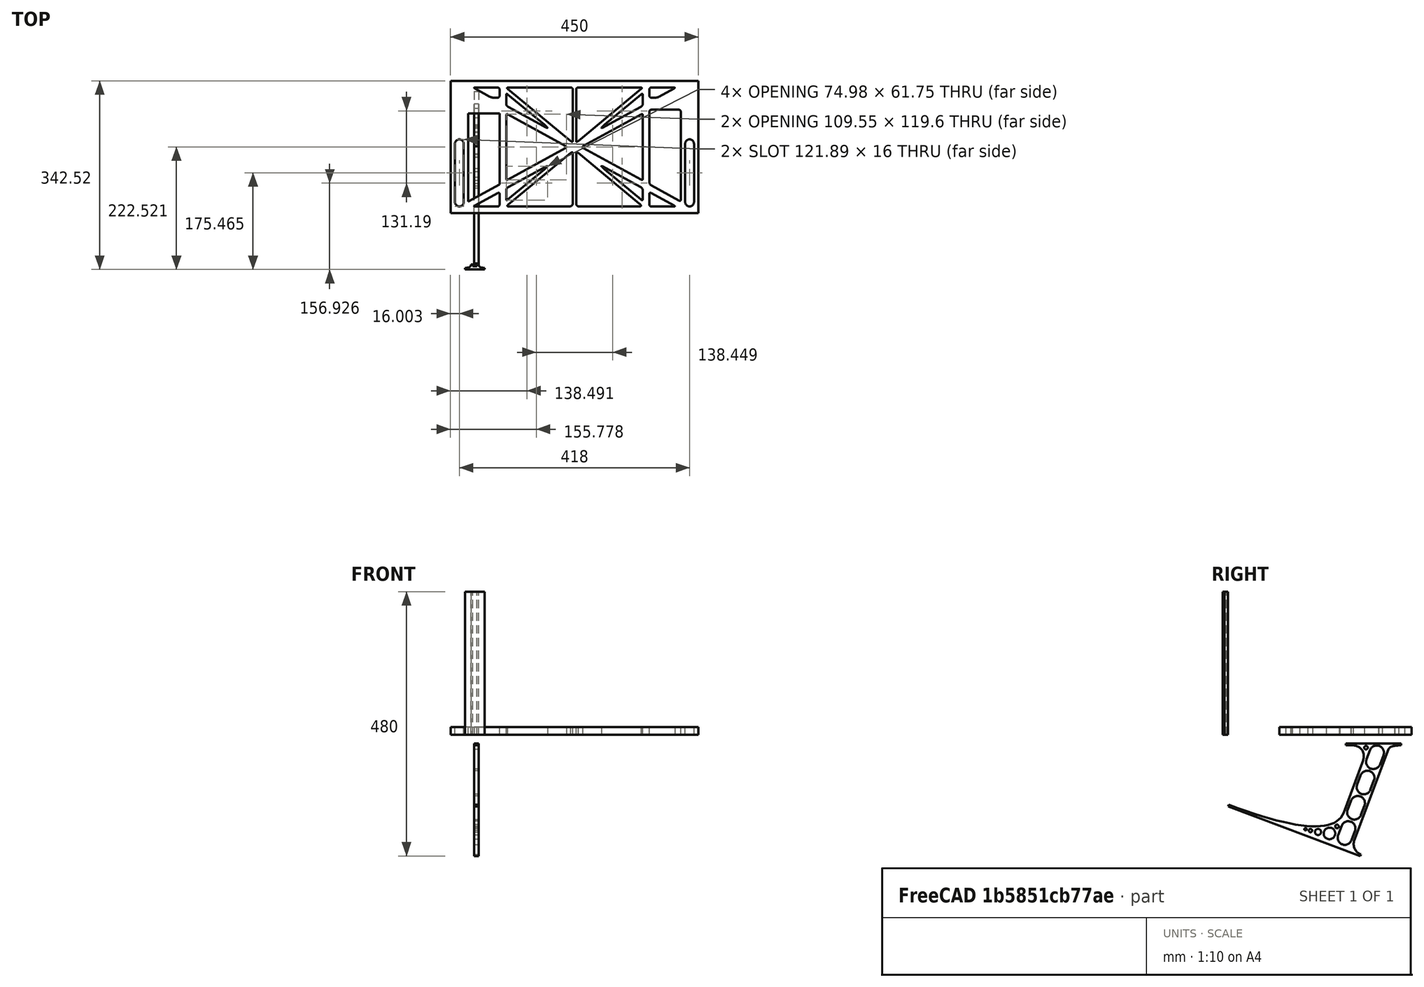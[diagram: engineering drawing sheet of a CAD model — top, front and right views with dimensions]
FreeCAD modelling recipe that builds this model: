
FCSTD DOCUMENT  (FreeCAD 0.19R0.19.2)
Label: laptopStand133FCStd
License: All rights reserved
LicenseURL: http://en.wikipedia.org/wiki/All_rights_reserved
objects: Sketcher::SketchObject×3, Part::Extrusion×3
note: 6 computed .brp shape members not serialized (recipe doc carries the construction recipe); baked Part::Feature solids carry a one-line shape summary decoded from their .brp

FEATURE [Sketcher::SketchObject] Sketch
  FullyConstrained = false
  sketch-geometry (349):
    g0: LineSegment StartX=-10.9272 StartY=-82.7794 StartZ=0 EndX=46.0728 EndY=-51.4823 EndZ=0
    g1: LineSegment StartX=-10.9272 StartY=76.4095 StartZ=0 EndX=-10.9272 EndY=-82.7794 EndZ=0
    g2: LineSegment StartX=46.0728 StartY=76.4095 StartZ=0 EndX=46.0728 EndY=-51.4823 EndZ=0
    g3: LineSegment StartX=-42.9272 StartY=136.221 StartZ=0 EndX=-42.9272 EndY=-103.779 EndZ=0
    g4: LineSegment StartX=407.073 StartY=136.221 StartZ=0 EndX=407.073 EndY=-103.779 EndZ=0
    g5: ArcOfCircle CenterX=-26.9272 CenterY=22.1087 CenterZ=0 NormalX=0 NormalY=0 NormalZ=1 AngleXU=0 Radius=8 StartAngle=1e-16 EndAngle=3.14159
    g6: ArcOfCircle CenterX=-26.9272 CenterY=-83.7794 CenterZ=0 NormalX=0 NormalY=0 NormalZ=1 AngleXU=0 Radius=8 StartAngle=3.14159 EndAngle=6.28319
    g7: LineSegment StartX=-34.9272 StartY=22.1087 StartZ=0 EndX=-34.9272 EndY=-83.7794 EndZ=0
    g8: LineSegment StartX=-18.9272 StartY=22.1087 StartZ=0 EndX=-18.9272 EndY=-83.7794 EndZ=0
    g9: ArcOfCircle CenterX=391.073 CenterY=22.1087 CenterZ=0 NormalX=0 NormalY=0 NormalZ=1 AngleXU=0 Radius=8 StartAngle=-4.4e-15 EndAngle=3.14159
    g10: LineSegment StartX=399.073 StartY=22.1087 StartZ=0 EndX=399.073 EndY=-83.7794 EndZ=0
    g11: LineSegment StartX=383.073 StartY=22.1087 StartZ=0 EndX=383.073 EndY=-83.7794 EndZ=0
    g12: ArcOfCircle CenterX=391.073 CenterY=-83.7794 CenterZ=0 NormalX=0 NormalY=0 NormalZ=1 AngleXU=0 Radius=8 StartAngle=3.14159 EndAngle=6.28319
    g13: Circle CenterX=175.022 CenterY=27.0628 CenterZ=0 NormalX=0 NormalY=0 NormalZ=1 AngleXU=0 Radius=1
    g14: Circle CenterX=179.022 CenterY=24.8665 CenterZ=0 NormalX=0 NormalY=0 NormalZ=1 AngleXU=0 Radius=1
    g15: Circle CenterX=179.022 CenterY=27.0628 CenterZ=0 NormalX=0 NormalY=0 NormalZ=1 AngleXU=0 Radius=1
    g16: BSplineCurve PolesCount=3 KnotsCount=2 Degree=2 IsPeriodic=0
    g17: GeomPoint X=175.022 Y=27.0628 Z=0
    g18: GeomPoint X=179.022 Y=27.0628 Z=0
    g19: Circle CenterX=189.124 CenterY=27.0628 CenterZ=0 NormalX=0 NormalY=0 NormalZ=1 AngleXU=0 Radius=1
    g20: Circle CenterX=185.124 CenterY=24.8665 CenterZ=0 NormalX=0 NormalY=0 NormalZ=1 AngleXU=0 Radius=1
    g21: Circle CenterX=185.124 CenterY=27.0628 CenterZ=0 NormalX=0 NormalY=0 NormalZ=1 AngleXU=0 Radius=1
    g22: BSplineCurve PolesCount=3 KnotsCount=2 Degree=2 IsPeriodic=0
    g23: GeomPoint X=189.124 Y=27.0628 Z=0
    g24: GeomPoint X=185.124 Y=27.0628 Z=0
    g25: Circle CenterX=175.022 CenterY=5.37834 CenterZ=0 NormalX=0 NormalY=0 NormalZ=1 AngleXU=0 Radius=1
    g26: Circle CenterX=179.022 CenterY=7.57463 CenterZ=0 NormalX=0 NormalY=0 NormalZ=1 AngleXU=0 Radius=1
    g27: Circle CenterX=179.022 CenterY=5.34704 CenterZ=0 NormalX=0 NormalY=0 NormalZ=1 AngleXU=0 Radius=1
    g28: BSplineCurve PolesCount=3 KnotsCount=2 Degree=2 IsPeriodic=0
    g29: GeomPoint X=175.022 Y=5.37834 Z=0
    g30: GeomPoint X=179.022 Y=5.34704 Z=0
    g31: Circle CenterX=189.124 CenterY=5.37834 CenterZ=0 NormalX=0 NormalY=0 NormalZ=1 AngleXU=0 Radius=1
    g32: Circle CenterX=185.124 CenterY=7.57463 CenterZ=0 NormalX=0 NormalY=0 NormalZ=1 AngleXU=0 Radius=1
    g33: Circle CenterX=185.124 CenterY=5.34704 CenterZ=0 NormalX=0 NormalY=0 NormalZ=1 AngleXU=0 Radius=1
    g34: BSplineCurve PolesCount=3 KnotsCount=2 Degree=2 IsPeriodic=0
    g35: GeomPoint X=189.124 Y=5.37834 Z=0
    g36: GeomPoint X=185.124 Y=5.34704 Z=0
    g37: Circle CenterX=165.871 CenterY=18.1458 CenterZ=0 NormalX=0 NormalY=0 NormalZ=1 AngleXU=0 Radius=1
    g38: Circle CenterX=169.377 CenterY=16.2206 CenterZ=0 NormalX=0 NormalY=0 NormalZ=1 AngleXU=0 Radius=1
    g39: Circle CenterX=165.871 CenterY=14.2954 CenterZ=0 NormalX=0 NormalY=0 NormalZ=1 AngleXU=0 Radius=1
    g40: BSplineCurve PolesCount=3 KnotsCount=2 Degree=2 IsPeriodic=0
    g41: GeomPoint X=165.871 Y=18.1458 Z=0
    g42: GeomPoint X=165.871 Y=14.2954 Z=0
    g43: Circle CenterX=198.275 CenterY=18.1458 CenterZ=0 NormalX=0 NormalY=0 NormalZ=1 AngleXU=0 Radius=1
    g44: Circle CenterX=194.768 CenterY=16.2206 CenterZ=0 NormalX=0 NormalY=0 NormalZ=1 AngleXU=0 Radius=1
    g45: Circle CenterX=198.275 CenterY=14.2954 CenterZ=0 NormalX=0 NormalY=0 NormalZ=1 AngleXU=0 Radius=1
    g46: BSplineCurve PolesCount=3 KnotsCount=2 Degree=2 IsPeriodic=0
    g47: GeomPoint X=198.275 Y=18.1458 Z=0
    g48: GeomPoint X=198.275 Y=14.2954 Z=0
    g49: LineSegment StartX=407.073 StartY=-103.779 StartZ=0 EndX=-42.9272 EndY=-103.779 EndZ=0
    g50: LineSegment StartX=407.073 StartY=136.221 StartZ=0 EndX=-42.9272 EndY=136.221 EndZ=0
    g51: LineSegment StartX=46.0728 StartY=76.4095 StartZ=0 EndX=-10.9272 EndY=76.4095 EndZ=0
    g52: Circle CenterX=125.607 CenterY=54.1951 CenterZ=0 NormalX=0 NormalY=0 NormalZ=1 AngleXU=0 Radius=1
    g53: Circle CenterX=139.632 CenterY=46.4944 CenterZ=0 NormalX=0 NormalY=0 NormalZ=1 AngleXU=0 Radius=1
    g54: Circle CenterX=127.326 CenterY=56.7187 CenterZ=0 NormalX=0 NormalY=0 NormalZ=1 AngleXU=0 Radius=1
    g55: BSplineCurve PolesCount=3 KnotsCount=2 Degree=2 IsPeriodic=0
    g56: GeomPoint X=125.607 Y=54.1951 Z=0
    g57: GeomPoint X=127.326 Y=56.7187 Z=0
    g58: Circle CenterX=236.821 CenterY=56.7187 CenterZ=0 NormalX=0 NormalY=0 NormalZ=1 AngleXU=0 Radius=1
    g59: Circle CenterX=224.513 CenterY=46.4944 CenterZ=0 NormalX=0 NormalY=0 NormalZ=1 AngleXU=0 Radius=1
    g60: Circle CenterX=238.538 CenterY=54.1951 CenterZ=0 NormalX=0 NormalY=0 NormalZ=1 AngleXU=0 Radius=1
    g61: BSplineCurve PolesCount=3 KnotsCount=2 Degree=2 IsPeriodic=0
    g62: GeomPoint X=236.821 Y=56.7187 Z=0
    g63: GeomPoint X=238.538 Y=54.1951 Z=0
    g64: Circle CenterX=238.538 CenterY=-21.7539 CenterZ=0 NormalX=0 NormalY=0 NormalZ=1 AngleXU=0 Radius=1
    g65: Circle CenterX=224.513 CenterY=-14.0532 CenterZ=0 NormalX=0 NormalY=0 NormalZ=1 AngleXU=0 Radius=1
    g66: Circle CenterX=236.821 CenterY=-24.2775 CenterZ=0 NormalX=0 NormalY=0 NormalZ=1 AngleXU=0 Radius=1
    g67: BSplineCurve PolesCount=3 KnotsCount=2 Degree=2 IsPeriodic=0
    g68: GeomPoint X=238.538 Y=-21.7539 Z=0
    g69: GeomPoint X=236.821 Y=-24.2775 Z=0
    g70: Circle CenterX=125.607 CenterY=-21.7539 CenterZ=0 NormalX=0 NormalY=0 NormalZ=1 AngleXU=0 Radius=1
    g71: Circle CenterX=139.632 CenterY=-14.0532 CenterZ=0 NormalX=0 NormalY=0 NormalZ=1 AngleXU=0 Radius=1
    g72: Circle CenterX=127.325 CenterY=-24.2775 CenterZ=0 NormalX=0 NormalY=0 NormalZ=1 AngleXU=0 Radius=1
    g73: BSplineCurve PolesCount=3 KnotsCount=2 Degree=2 IsPeriodic=0
    g74: GeomPoint X=125.607 Y=-21.7539 Z=0
    g75: GeomPoint X=127.325 Y=-24.2775 Z=0
    g76: Circle CenterX=302.996 CenterY=111.695 CenterZ=0 NormalX=0 NormalY=0 NormalZ=1 AngleXU=0 Radius=1
    g77: Circle CenterX=306.073 CenterY=114.251 CenterZ=0 NormalX=0 NormalY=0 NormalZ=1 AngleXU=0 Radius=1
    g78: Circle CenterX=306.073 CenterY=110.251 CenterZ=0 NormalX=0 NormalY=0 NormalZ=1 AngleXU=0 Radius=1
    g79: BSplineCurve PolesCount=3 KnotsCount=2 Degree=2 IsPeriodic=0
    g80: GeomPoint X=302.996 Y=111.695 Z=0
    g81: GeomPoint X=306.073 Y=110.251 Z=0
    g82: Circle CenterX=306.073 CenterY=95.2763 CenterZ=0 NormalX=0 NormalY=0 NormalZ=1 AngleXU=0 Radius=1
    g83: Circle CenterX=306.073 CenterY=91.2763 CenterZ=0 NormalX=0 NormalY=0 NormalZ=1 AngleXU=0 Radius=1
    g84: Circle CenterX=302.567 CenterY=89.3511 CenterZ=0 NormalX=0 NormalY=0 NormalZ=1 AngleXU=0 Radius=1
    g85: BSplineCurve PolesCount=3 KnotsCount=2 Degree=2 IsPeriodic=0
    g86: GeomPoint X=306.073 Y=95.2763 Z=0
    g87: GeomPoint X=302.567 Y=89.3511 Z=0
    g88: LineSegment StartX=306.073 StartY=110.251 StartZ=0 EndX=306.073 EndY=95.2763 EndZ=0
    g89: LineSegment StartX=302.996 StartY=111.695 StartZ=0 EndX=236.821 EndY=56.7187 EndZ=0
    g90: LineSegment StartX=238.538 StartY=54.1951 StartZ=0 EndX=302.567 EndY=89.3511 EndZ=0
    g91: Circle CenterX=61.1496 CenterY=111.695 CenterZ=0 NormalX=0 NormalY=0 NormalZ=1 AngleXU=0 Radius=1
    g92: Circle CenterX=58.0728 CenterY=114.251 CenterZ=0 NormalX=0 NormalY=0 NormalZ=1 AngleXU=0 Radius=1
    g93: Circle CenterX=58.0728 CenterY=110.251 CenterZ=0 NormalX=0 NormalY=0 NormalZ=1 AngleXU=0 Radius=1
    g94: BSplineCurve PolesCount=3 KnotsCount=2 Degree=2 IsPeriodic=0
    g95: GeomPoint X=61.1496 Y=111.695 Z=0
    g96: GeomPoint X=58.0728 Y=110.251 Z=0
    g97: Circle CenterX=61.5791 CenterY=89.3511 CenterZ=0 NormalX=0 NormalY=0 NormalZ=1 AngleXU=0 Radius=1
    g98: Circle CenterX=58.0728 CenterY=91.2763 CenterZ=0 NormalX=0 NormalY=0 NormalZ=1 AngleXU=0 Radius=1
    g99: Circle CenterX=58.0728 CenterY=95.2763 CenterZ=0 NormalX=0 NormalY=0 NormalZ=1 AngleXU=0 Radius=1
    g100: BSplineCurve PolesCount=3 KnotsCount=2 Degree=2 IsPeriodic=0
    g101: GeomPoint X=61.5791 Y=89.3511 Z=0
    g102: GeomPoint X=58.0728 Y=95.2763 Z=0
    g103: LineSegment StartX=58.0728 StartY=110.251 StartZ=0 EndX=58.0728 EndY=95.2763 EndZ=0
    g104: LineSegment StartX=61.1496 StartY=111.695 StartZ=0 EndX=127.326 EndY=56.7187 EndZ=0
    g105: LineSegment StartX=125.607 StartY=54.1951 StartZ=0 EndX=61.5791 EndY=89.3511 EndZ=0
    g106: Circle CenterX=61.5791 CenterY=-56.9099 CenterZ=0 NormalX=0 NormalY=0 NormalZ=1 AngleXU=0 Radius=1
    g107: Circle CenterX=58.0728 CenterY=-58.8351 CenterZ=0 NormalX=0 NormalY=0 NormalZ=1 AngleXU=0 Radius=1
    g108: Circle CenterX=58.0728 CenterY=-62.8351 CenterZ=0 NormalX=0 NormalY=0 NormalZ=1 AngleXU=0 Radius=1
    g109: BSplineCurve PolesCount=3 KnotsCount=2 Degree=2 IsPeriodic=0
    g110: GeomPoint X=61.5791 Y=-56.9099 Z=0
    g111: GeomPoint X=58.0728 Y=-62.8351 Z=0
    g112: Circle CenterX=58.0728 CenterY=-77.8102 CenterZ=0 NormalX=0 NormalY=0 NormalZ=1 AngleXU=0 Radius=1
    g113: Circle CenterX=58.0728 CenterY=-81.8102 CenterZ=0 NormalX=0 NormalY=0 NormalZ=1 AngleXU=0 Radius=1
    g114: Circle CenterX=61.1496 CenterY=-79.2541 CenterZ=0 NormalX=0 NormalY=0 NormalZ=1 AngleXU=0 Radius=1
    g115: BSplineCurve PolesCount=3 KnotsCount=2 Degree=2 IsPeriodic=0
    g116: GeomPoint X=58.0728 Y=-77.8102 Z=0
    g117: GeomPoint X=61.1496 Y=-79.2541 Z=0
    g118: LineSegment StartX=58.0728 StartY=-62.8351 StartZ=0 EndX=58.0728 EndY=-77.8102 EndZ=0
    g119: LineSegment StartX=61.1496 StartY=-79.2541 StartZ=0 EndX=127.325 EndY=-24.2775 EndZ=0
    g120: LineSegment StartX=125.607 StartY=-21.7539 StartZ=0 EndX=61.5791 EndY=-56.9099 EndZ=0
    g121: Circle CenterX=302.567 CenterY=-56.9099 CenterZ=0 NormalX=0 NormalY=0 NormalZ=1 AngleXU=0 Radius=1
    g122: Circle CenterX=306.073 CenterY=-58.8351 CenterZ=0 NormalX=0 NormalY=0 NormalZ=1 AngleXU=0 Radius=1
    g123: Circle CenterX=306.073 CenterY=-62.8351 CenterZ=0 NormalX=0 NormalY=0 NormalZ=1 AngleXU=0 Radius=1
    g124: BSplineCurve PolesCount=3 KnotsCount=2 Degree=2 IsPeriodic=0
    g125: GeomPoint X=302.567 Y=-56.9099 Z=0
    g126: GeomPoint X=306.073 Y=-62.8351 Z=0
    g127: Circle CenterX=302.996 CenterY=-79.2541 CenterZ=0 NormalX=0 NormalY=0 NormalZ=1 AngleXU=0 Radius=1
    g128: Circle CenterX=306.073 CenterY=-81.8102 CenterZ=0 NormalX=0 NormalY=0 NormalZ=1 AngleXU=0 Radius=1
    g129: Circle CenterX=306.073 CenterY=-77.8102 CenterZ=0 NormalX=0 NormalY=0 NormalZ=1 AngleXU=0 Radius=1
    g130: BSplineCurve PolesCount=3 KnotsCount=2 Degree=2 IsPeriodic=0
    g131: GeomPoint X=302.996 Y=-79.2541 Z=0
    g132: GeomPoint X=306.073 Y=-77.8102 Z=0
    g133: LineSegment StartX=306.073 StartY=-62.8351 StartZ=0 EndX=306.073 EndY=-77.8102 EndZ=0
    g134: LineSegment StartX=302.996 StartY=-79.2541 StartZ=0 EndX=236.821 EndY=-24.2775 EndZ=0
    g135: LineSegment StartX=238.538 StartY=-21.7539 StartZ=0 EndX=302.567 EndY=-56.9099 EndZ=0
    g136: Circle CenterX=61.6457 CenterY=-88.8112 CenterZ=0 NormalX=0 NormalY=0 NormalZ=1 AngleXU=0 Radius=1
    g137: Circle CenterX=58.0728 CenterY=-91.7794 CenterZ=0 NormalX=0 NormalY=0 NormalZ=1 AngleXU=0 Radius=1
    g138: Circle CenterX=63.9135 CenterY=-91.7794 CenterZ=0 NormalX=0 NormalY=0 NormalZ=1 AngleXU=0 Radius=1
    g139: BSplineCurve PolesCount=3 KnotsCount=2 Degree=2 IsPeriodic=0
    g140: GeomPoint X=61.6457 Y=-88.8112 Z=0
    g141: GeomPoint X=63.9135 Y=-91.7794 Z=0
    g142: Circle CenterX=179.022 CenterY=-85.8163 CenterZ=0 NormalX=0 NormalY=0 NormalZ=1 AngleXU=0 Radius=1
    g143: Circle CenterX=179.022 CenterY=-91.7794 CenterZ=0 NormalX=0 NormalY=0 NormalZ=1 AngleXU=0 Radius=1
    g144: Circle CenterX=171.895 CenterY=-91.7794 CenterZ=0 NormalX=0 NormalY=0 NormalZ=1 AngleXU=0 Radius=1
    g145: BSplineCurve PolesCount=3 KnotsCount=2 Degree=2 IsPeriodic=0
    g146: GeomPoint X=179.022 Y=-85.8163 Z=0
    g147: GeomPoint X=171.895 Y=-91.7794 Z=0
    g148: Circle CenterX=185.124 CenterY=-86.2028 CenterZ=0 NormalX=0 NormalY=0 NormalZ=1 AngleXU=0 Radius=1
    g149: Circle CenterX=185.124 CenterY=-91.7794 CenterZ=0 NormalX=0 NormalY=0 NormalZ=1 AngleXU=0 Radius=1
    g150: Circle CenterX=191.747 CenterY=-91.7794 CenterZ=0 NormalX=0 NormalY=0 NormalZ=1 AngleXU=0 Radius=1
    g151: BSplineCurve PolesCount=3 KnotsCount=2 Degree=2 IsPeriodic=0
    g152: GeomPoint X=185.124 Y=-86.2028 Z=0
    g153: GeomPoint X=191.747 Y=-91.7794 Z=0
    g154: Circle CenterX=299.888 CenterY=-86.6413 CenterZ=0 NormalX=0 NormalY=0 NormalZ=1 AngleXU=0 Radius=1
    g155: Circle CenterX=306.073 CenterY=-91.7794 CenterZ=0 NormalX=0 NormalY=0 NormalZ=1 AngleXU=0 Radius=1
    g156: Circle CenterX=298.776 CenterY=-91.7794 CenterZ=0 NormalX=0 NormalY=0 NormalZ=1 AngleXU=0 Radius=1
    g157: BSplineCurve PolesCount=3 KnotsCount=2 Degree=2 IsPeriodic=0
    g158: GeomPoint X=299.888 Y=-86.6413 Z=0
    g159: GeomPoint X=298.776 Y=-91.7794 Z=0
    g160: LineSegment StartX=189.124 StartY=5.37834 StartZ=0 EndX=299.888 EndY=-86.6413 EndZ=0
    g161: LineSegment StartX=298.776 StartY=-91.7794 StartZ=0 EndX=191.747 EndY=-91.7794 EndZ=0
    g162: LineSegment StartX=185.124 StartY=-86.2028 StartZ=0 EndX=185.124 EndY=5.34704 EndZ=0
    g163: LineSegment StartX=179.022 StartY=5.34704 StartZ=0 EndX=179.022 EndY=-85.8163 EndZ=0
    g164: LineSegment StartX=171.895 StartY=-91.7794 StartZ=0 EndX=63.9135 EndY=-91.7794 EndZ=0
    g165: LineSegment StartX=61.6457 StartY=-88.8112 StartZ=0 EndX=175.022 EndY=5.37834 EndZ=0
    g166: Circle CenterX=302.073 CenterY=124.221 CenterZ=0 NormalX=0 NormalY=0 NormalZ=1 AngleXU=0 Radius=1
    g167: Circle CenterX=306.073 CenterY=124.221 CenterZ=0 NormalX=0 NormalY=0 NormalZ=1 AngleXU=0 Radius=1
    g168: Circle CenterX=302.996 CenterY=121.665 CenterZ=0 NormalX=0 NormalY=0 NormalZ=1 AngleXU=0 Radius=1
    g169: BSplineCurve PolesCount=3 KnotsCount=2 Degree=2 IsPeriodic=0
    g170: GeomPoint X=302.073 Y=124.221 Z=0
    g171: GeomPoint X=302.996 Y=121.665 Z=0
    g172: Circle CenterX=189.124 CenterY=124.221 CenterZ=0 NormalX=0 NormalY=0 NormalZ=1 AngleXU=0 Radius=1
    g173: Circle CenterX=185.124 CenterY=124.221 CenterZ=0 NormalX=0 NormalY=0 NormalZ=1 AngleXU=0 Radius=1
    g174: Circle CenterX=185.124 CenterY=120.221 CenterZ=0 NormalX=0 NormalY=0 NormalZ=1 AngleXU=0 Radius=1
    g175: BSplineCurve PolesCount=3 KnotsCount=2 Degree=2 IsPeriodic=0
    g176: GeomPoint X=189.124 Y=124.221 Z=0
    g177: GeomPoint X=185.124 Y=120.221 Z=0
    g178: Circle CenterX=175.022 CenterY=124.221 CenterZ=0 NormalX=0 NormalY=0 NormalZ=1 AngleXU=0 Radius=1
    g179: Circle CenterX=179.022 CenterY=124.221 CenterZ=0 NormalX=0 NormalY=0 NormalZ=1 AngleXU=0 Radius=1
    g180: Circle CenterX=179.022 CenterY=120.221 CenterZ=0 NormalX=0 NormalY=0 NormalZ=1 AngleXU=0 Radius=1
    g181: BSplineCurve PolesCount=3 KnotsCount=2 Degree=2 IsPeriodic=0
    g182: GeomPoint X=175.022 Y=124.221 Z=0
    g183: GeomPoint X=179.022 Y=120.221 Z=0
    g184: Circle CenterX=62.0728 CenterY=124.221 CenterZ=0 NormalX=0 NormalY=0 NormalZ=1 AngleXU=0 Radius=1
    g185: Circle CenterX=58.0728 CenterY=124.221 CenterZ=0 NormalX=0 NormalY=0 NormalZ=1 AngleXU=0 Radius=1
    g186: Circle CenterX=61.1496 CenterY=121.665 CenterZ=0 NormalX=0 NormalY=0 NormalZ=1 AngleXU=0 Radius=1
    g187: BSplineCurve PolesCount=3 KnotsCount=2 Degree=2 IsPeriodic=0
    g188: GeomPoint X=62.0728 Y=124.221 Z=0
    g189: GeomPoint X=61.1496 Y=121.665 Z=0
    g190: LineSegment StartX=62.0728 StartY=124.221 StartZ=0 EndX=175.022 EndY=124.221 EndZ=0
    g191: LineSegment StartX=179.022 StartY=120.221 StartZ=0 EndX=179.022 EndY=27.0628 EndZ=0
    g192: LineSegment StartX=185.124 StartY=27.0628 StartZ=0 EndX=185.124 EndY=120.221 EndZ=0
    g193: LineSegment StartX=189.124 StartY=124.221 StartZ=0 EndX=302.073 EndY=124.221 EndZ=0
    g194: LineSegment StartX=302.996 StartY=121.665 StartZ=0 EndX=189.124 EndY=27.0628 EndZ=0
    g195: LineSegment StartX=175.022 StartY=27.0628 StartZ=0 EndX=61.1496 EndY=121.665 EndZ=0
    g196: Circle CenterX=61.5791 CenterY=75.4095 CenterZ=0 NormalX=0 NormalY=0 NormalZ=1 AngleXU=0 Radius=1
    g197: Circle CenterX=58.0728 CenterY=77.3346 CenterZ=0 NormalX=0 NormalY=0 NormalZ=1 AngleXU=0 Radius=1
    g198: Circle CenterX=58.0728 CenterY=73.3346 CenterZ=0 NormalX=0 NormalY=0 NormalZ=1 AngleXU=0 Radius=1
    g199: BSplineCurve PolesCount=3 KnotsCount=2 Degree=2 IsPeriodic=0
    g200: GeomPoint X=61.5791 Y=75.4095 Z=0
    g201: GeomPoint X=58.0728 Y=73.3346 Z=0
    g202: Circle CenterX=58.0728 CenterY=-40.8935 CenterZ=0 NormalX=0 NormalY=0 NormalZ=1 AngleXU=0 Radius=1
    g203: Circle CenterX=58.0728 CenterY=-44.8935 CenterZ=0 NormalX=0 NormalY=0 NormalZ=1 AngleXU=0 Radius=1
    g204: Circle CenterX=61.5791 CenterY=-42.9683 CenterZ=0 NormalX=0 NormalY=0 NormalZ=1 AngleXU=0 Radius=1
    g205: BSplineCurve PolesCount=3 KnotsCount=2 Degree=2 IsPeriodic=0
    g206: GeomPoint X=58.0728 Y=-40.8935 Z=0
    g207: GeomPoint X=61.5791 Y=-42.9683 Z=0
    g208: LineSegment StartX=61.5791 StartY=-42.9683 StartZ=0 EndX=165.871 EndY=14.2954 EndZ=0
    g209: LineSegment StartX=165.871 StartY=18.1458 StartZ=0 EndX=61.5791 EndY=75.4095 EndZ=0
    g210: LineSegment StartX=58.0728 StartY=73.3346 StartZ=0 EndX=58.0728 EndY=-40.8935 EndZ=0
    g211: Circle CenterX=302.567 CenterY=-42.9683 CenterZ=0 NormalX=0 NormalY=0 NormalZ=1 AngleXU=0 Radius=1
    g212: Circle CenterX=306.073 CenterY=-44.8935 CenterZ=0 NormalX=0 NormalY=0 NormalZ=1 AngleXU=0 Radius=1
    g213: Circle CenterX=306.073 CenterY=-40.8935 CenterZ=0 NormalX=0 NormalY=0 NormalZ=1 AngleXU=0 Radius=1
    g214: BSplineCurve PolesCount=3 KnotsCount=2 Degree=2 IsPeriodic=0
    g215: GeomPoint X=302.567 Y=-42.9683 Z=0
    g216: GeomPoint X=306.073 Y=-40.8935 Z=0
    g217: Circle CenterX=306.073 CenterY=73.3346 CenterZ=0 NormalX=0 NormalY=0 NormalZ=1 AngleXU=0 Radius=1
    g218: Circle CenterX=306.073 CenterY=77.3346 CenterZ=0 NormalX=0 NormalY=0 NormalZ=1 AngleXU=0 Radius=1
    g219: Circle CenterX=302.567 CenterY=75.4095 CenterZ=0 NormalX=0 NormalY=0 NormalZ=1 AngleXU=0 Radius=1
    g220: BSplineCurve PolesCount=3 KnotsCount=2 Degree=2 IsPeriodic=0
    g221: GeomPoint X=306.073 Y=73.3346 Z=0
    g222: GeomPoint X=302.567 Y=75.4095 Z=0
    g223: LineSegment StartX=302.567 StartY=-42.9683 StartZ=0 EndX=198.275 EndY=14.2954 EndZ=0
    g224: LineSegment StartX=198.275 StartY=18.1458 StartZ=0 EndX=302.567 EndY=75.4095 EndZ=0
    g225: LineSegment StartX=306.073 StartY=73.3346 StartZ=0 EndX=306.073 EndY=-40.8935 EndZ=0
    g226: LineSegment StartX=322.073 StartY=105.865 StartZ=0 EndX=328.643 EndY=105.865 EndZ=0
    g227: LineSegment StartX=318.073 StartY=120.221 StartZ=0 EndX=318.073 EndY=109.865 EndZ=0
    g228: LineSegment StartX=336.157 StartY=107.779 StartZ=0 EndX=362.567 EndY=122.294 EndZ=0
    g229: Circle CenterX=362.073 CenterY=124.221 CenterZ=0 NormalX=0 NormalY=0 NormalZ=1 AngleXU=0 Radius=1
    g230: Circle CenterX=366.073 CenterY=124.221 CenterZ=0 NormalX=0 NormalY=0 NormalZ=1 AngleXU=0 Radius=1
    g231: Circle CenterX=362.567 CenterY=122.294 CenterZ=0 NormalX=0 NormalY=0 NormalZ=1 AngleXU=0 Radius=1
    g232: BSplineCurve PolesCount=3 KnotsCount=2 Degree=2 IsPeriodic=0
    g233: GeomPoint X=362.073 Y=124.221 Z=0
    g234: GeomPoint X=362.567 Y=122.294 Z=0
    g235: Circle CenterX=322.073 CenterY=124.221 CenterZ=0 NormalX=0 NormalY=0 NormalZ=1 AngleXU=0 Radius=1
    g236: Circle CenterX=318.073 CenterY=124.221 CenterZ=0 NormalX=0 NormalY=0 NormalZ=1 AngleXU=0 Radius=1
    g237: Circle CenterX=318.073 CenterY=120.221 CenterZ=0 NormalX=0 NormalY=0 NormalZ=1 AngleXU=0 Radius=1
    g238: BSplineCurve PolesCount=3 KnotsCount=2 Degree=2 IsPeriodic=0
    g239: GeomPoint X=322.073 Y=124.221 Z=0
    g240: GeomPoint X=318.073 Y=120.221 Z=0
    g241: Circle CenterX=322.073 CenterY=105.865 CenterZ=0 NormalX=0 NormalY=0 NormalZ=1 AngleXU=0 Radius=1
    g242: Circle CenterX=318.073 CenterY=105.865 CenterZ=0 NormalX=0 NormalY=0 NormalZ=1 AngleXU=0 Radius=1
    g243: Circle CenterX=318.073 CenterY=109.865 CenterZ=0 NormalX=0 NormalY=0 NormalZ=1 AngleXU=0 Radius=1
    g244: BSplineCurve PolesCount=3 KnotsCount=2 Degree=2 IsPeriodic=0
    g245: GeomPoint X=322.073 Y=105.865 Z=0
    g246: GeomPoint X=318.073 Y=109.865 Z=0
    g247: Circle CenterX=336.157 CenterY=107.779 CenterZ=0 NormalX=0 NormalY=0 NormalZ=1 AngleXU=0 Radius=1
    g248: Circle CenterX=332.651 CenterY=105.853 CenterZ=0 NormalX=0 NormalY=0 NormalZ=1 AngleXU=0 Radius=1
    g249: Circle CenterX=328.643 CenterY=105.865 CenterZ=0 NormalX=0 NormalY=0 NormalZ=1 AngleXU=0 Radius=1
    g250: BSplineCurve PolesCount=3 KnotsCount=2 Degree=2 IsPeriodic=0
    g251: GeomPoint X=336.157 Y=107.779 Z=0
    g252: GeomPoint X=328.643 Y=105.865 Z=0
    g253: LineSegment StartX=322.073 StartY=124.221 StartZ=0 EndX=362.073 EndY=124.221 EndZ=0
    g254: Circle CenterX=371.567 CenterY=-80.8644 CenterZ=0 NormalX=0 NormalY=0 NormalZ=1 AngleXU=0 Radius=1
    g255: Circle CenterX=375.073 CenterY=-82.7896 CenterZ=0 NormalX=0 NormalY=0 NormalZ=1 AngleXU=0 Radius=1
    g256: Circle CenterX=375.073 CenterY=-78.7896 CenterZ=0 NormalX=0 NormalY=0 NormalZ=1 AngleXU=0 Radius=1
    g257: BSplineCurve PolesCount=3 KnotsCount=2 Degree=2 IsPeriodic=0
    g258: GeomPoint X=371.567 Y=-80.8644 Z=0
    g259: GeomPoint X=375.073 Y=-78.7896 Z=0
    g260: Circle CenterX=321.579 CenterY=-53.4075 CenterZ=0 NormalX=0 NormalY=0 NormalZ=1 AngleXU=0 Radius=1
    g261: Circle CenterX=318.073 CenterY=-51.4823 CenterZ=0 NormalX=0 NormalY=0 NormalZ=1 AngleXU=0 Radius=1
    g262: Circle CenterX=318.073 CenterY=-47.4823 CenterZ=0 NormalX=0 NormalY=0 NormalZ=1 AngleXU=0 Radius=1
    g263: BSplineCurve PolesCount=3 KnotsCount=2 Degree=2 IsPeriodic=0
    g264: GeomPoint X=321.579 Y=-53.4075 Z=0
    g265: GeomPoint X=318.073 Y=-47.4823 Z=0
    g266: LineSegment StartX=371.567 StartY=-80.8644 StartZ=0 EndX=321.579 EndY=-53.4075 EndZ=0
    g267: Circle CenterX=321.579 CenterY=-67.3492 CenterZ=0 NormalX=0 NormalY=0 NormalZ=1 AngleXU=0 Radius=1
    g268: Circle CenterX=318.073 CenterY=-65.424 CenterZ=0 NormalX=0 NormalY=0 NormalZ=1 AngleXU=0 Radius=1
    g269: Circle CenterX=318.073 CenterY=-69.424 CenterZ=0 NormalX=0 NormalY=0 NormalZ=1 AngleXU=0 Radius=1
    g270: BSplineCurve PolesCount=3 KnotsCount=2 Degree=2 IsPeriodic=0
    g271: GeomPoint X=321.579 Y=-67.3492 Z=0
    g272: GeomPoint X=318.073 Y=-69.424 Z=0
    g273: Circle CenterX=362.567 CenterY=-89.8542 CenterZ=0 NormalX=0 NormalY=0 NormalZ=1 AngleXU=0 Radius=1
    g274: Circle CenterX=366.073 CenterY=-91.7794 CenterZ=0 NormalX=0 NormalY=0 NormalZ=1 AngleXU=0 Radius=1
    g275: Circle CenterX=362.073 CenterY=-91.7794 CenterZ=0 NormalX=0 NormalY=0 NormalZ=1 AngleXU=0 Radius=1
    g276: BSplineCurve PolesCount=3 KnotsCount=2 Degree=2 IsPeriodic=0
    g277: GeomPoint X=362.567 Y=-89.8542 Z=0
    g278: GeomPoint X=362.073 Y=-91.7794 Z=0
    g279: Circle CenterX=322.073 CenterY=-91.7794 CenterZ=0 NormalX=0 NormalY=0 NormalZ=1 AngleXU=0 Radius=1
    g280: Circle CenterX=318.073 CenterY=-91.7794 CenterZ=0 NormalX=0 NormalY=0 NormalZ=1 AngleXU=0 Radius=1
    g281: Circle CenterX=318.073 CenterY=-87.7794 CenterZ=0 NormalX=0 NormalY=0 NormalZ=1 AngleXU=0 Radius=1
    g282: BSplineCurve PolesCount=3 KnotsCount=2 Degree=2 IsPeriodic=0
    g283: GeomPoint X=322.073 Y=-91.7794 Z=0
    g284: GeomPoint X=318.073 Y=-87.7794 Z=0
    g285: LineSegment StartX=362.567 StartY=-89.8542 StartZ=0 EndX=321.579 EndY=-67.3492 EndZ=0
    g286: LineSegment StartX=318.073 StartY=-69.424 StartZ=0 EndX=318.073 EndY=-87.7794 EndZ=0
    g287: LineSegment StartX=322.073 StartY=-91.7794 StartZ=0 EndX=362.073 EndY=-91.7794 EndZ=0
    g288: Circle CenterX=2.07281 CenterY=124.221 CenterZ=0 NormalX=0 NormalY=0 NormalZ=1 AngleXU=0 Radius=1
    g289: Circle CenterX=1.57905 CenterY=122.295 CenterZ=0 NormalX=0 NormalY=0 NormalZ=1 AngleXU=0 Radius=1
    g290: BSplineCurve PolesCount=3 KnotsCount=2 Degree=2 IsPeriodic=0
    g291: GeomPoint X=2.07281 Y=124.221 Z=0
    g292: GeomPoint X=1.57905 Y=122.295 Z=0
    g293: Circle CenterX=42.0728 CenterY=124.221 CenterZ=0 NormalX=0 NormalY=0 NormalZ=1 AngleXU=0 Radius=1
    g294: Circle CenterX=46.0728 CenterY=124.221 CenterZ=0 NormalX=0 NormalY=0 NormalZ=1 AngleXU=0 Radius=1
    g295: Circle CenterX=46.0728 CenterY=120.221 CenterZ=0 NormalX=0 NormalY=0 NormalZ=1 AngleXU=0 Radius=1
    g296: BSplineCurve PolesCount=3 KnotsCount=2 Degree=2 IsPeriodic=0
    g297: GeomPoint X=42.0728 Y=124.221 Z=0
    g298: GeomPoint X=46.0728 Y=120.221 Z=0
    g299: Circle CenterX=46.0728 CenterY=109.865 CenterZ=0 NormalX=0 NormalY=0 NormalZ=1 AngleXU=0 Radius=1
    g300: Circle CenterX=46.0728 CenterY=105.865 CenterZ=0 NormalX=0 NormalY=0 NormalZ=1 AngleXU=0 Radius=1
    g301: Circle CenterX=42.0728 CenterY=105.865 CenterZ=0 NormalX=0 NormalY=0 NormalZ=1 AngleXU=0 Radius=1
    g302: BSplineCurve PolesCount=3 KnotsCount=2 Degree=2 IsPeriodic=0
    g303: GeomPoint X=46.0728 Y=109.865 Z=0
    g304: GeomPoint X=42.0728 Y=105.865 Z=0
    g305: Circle CenterX=35.5028 CenterY=105.865 CenterZ=0 NormalX=0 NormalY=0 NormalZ=1 AngleXU=0 Radius=1
    g306: Circle CenterX=31.5028 CenterY=105.865 CenterZ=0 NormalX=0 NormalY=0 NormalZ=1 AngleXU=0 Radius=1
    g307: Circle CenterX=27.9965 CenterY=107.79 CenterZ=0 NormalX=0 NormalY=0 NormalZ=1 AngleXU=0 Radius=1
    g308: BSplineCurve PolesCount=3 KnotsCount=2 Degree=2 IsPeriodic=0
    g309: GeomPoint X=35.5028 Y=105.865 Z=0
    g310: GeomPoint X=27.9965 Y=107.79 Z=0
    g311: LineSegment StartX=2.07281 StartY=124.221 StartZ=0 EndX=42.0728 EndY=124.221 EndZ=0
    g312: LineSegment StartX=46.0728 StartY=120.221 StartZ=0 EndX=46.0728 EndY=109.865 EndZ=0
    g313: LineSegment StartX=42.0728 StartY=105.865 StartZ=0 EndX=35.5028 EndY=105.865 EndZ=0
    g314: LineSegment StartX=27.9965 StartY=107.79 StartZ=0 EndX=1.57905 EndY=122.295 EndZ=0
    g315: Circle CenterX=42.5666 CenterY=-67.3492 CenterZ=0 NormalX=0 NormalY=0 NormalZ=1 AngleXU=0 Radius=1
    g316: Circle CenterX=46.0728 CenterY=-65.424 CenterZ=0 NormalX=0 NormalY=0 NormalZ=1 AngleXU=0 Radius=1
    g317: Circle CenterX=46.0728 CenterY=-69.424 CenterZ=0 NormalX=0 NormalY=0 NormalZ=1 AngleXU=0 Radius=1
    g318: BSplineCurve PolesCount=3 KnotsCount=2 Degree=2 IsPeriodic=0
    g319: GeomPoint X=42.5666 Y=-67.3492 Z=0
    g320: GeomPoint X=46.0728 Y=-69.424 Z=0
    g321: Circle CenterX=46.0728 CenterY=-87.7794 CenterZ=0 NormalX=0 NormalY=0 NormalZ=1 AngleXU=0 Radius=1
    g322: Circle CenterX=46.0728 CenterY=-91.7794 CenterZ=0 NormalX=0 NormalY=0 NormalZ=1 AngleXU=0 Radius=1
    g323: Circle CenterX=42.0728 CenterY=-91.7794 CenterZ=0 NormalX=0 NormalY=0 NormalZ=1 AngleXU=0 Radius=1
    g324: BSplineCurve PolesCount=3 KnotsCount=2 Degree=2 IsPeriodic=0
    g325: GeomPoint X=46.0728 Y=-87.7794 Z=0
    g326: GeomPoint X=42.0728 Y=-91.7794 Z=0
    g327: Circle CenterX=2.07281 CenterY=-91.7794 CenterZ=0 NormalX=0 NormalY=0 NormalZ=1 AngleXU=0 Radius=1
    g328: Circle CenterX=-1.92719 CenterY=-91.7794 CenterZ=0 NormalX=0 NormalY=0 NormalZ=1 AngleXU=0 Radius=1
    g329: Circle CenterX=1.57905 CenterY=-89.8542 CenterZ=0 NormalX=0 NormalY=0 NormalZ=1 AngleXU=0 Radius=1
    g330: BSplineCurve PolesCount=3 KnotsCount=2 Degree=2 IsPeriodic=0
    g331: GeomPoint X=2.07281 Y=-91.7794 Z=0
    g332: GeomPoint X=1.57905 Y=-89.8542 Z=0
    g333: LineSegment StartX=2.07281 StartY=-91.7794 StartZ=0 EndX=42.0728 EndY=-91.7794 EndZ=0
    g334: LineSegment StartX=46.0728 StartY=-87.7794 StartZ=0 EndX=46.0728 EndY=-69.424 EndZ=0
    g335: LineSegment StartX=42.5666 StartY=-67.3492 StartZ=0 EndX=1.57905 EndY=-89.8542 EndZ=0
    g336: LineSegment StartX=375.073 StartY=76.4095 StartZ=0 EndX=375.073 EndY=-78.7896 EndZ=0
    g337: Circle CenterX=322.073 CenterY=76.4095 CenterZ=0 NormalX=0 NormalY=0 NormalZ=1 AngleXU=0 Radius=4
    g338: BSplineCurve PolesCount=3 KnotsCount=2 Degree=2 IsPeriodic=0
    g339: GeomPoint X=318.073 Y=72.4095 Z=0
    g340: GeomPoint X=322.073 Y=76.4095 Z=0
    g341: LineSegment StartX=371.073 StartY=76.4095 StartZ=0 EndX=375.073 EndY=76.4095 EndZ=0
    g342: Circle CenterX=375.073 CenterY=72.4095 CenterZ=0 NormalX=0 NormalY=0 NormalZ=1 AngleXU=0 Radius=1
    g343: Circle CenterX=375.073 CenterY=76.4095 CenterZ=0 NormalX=0 NormalY=0 NormalZ=1 AngleXU=0 Radius=1
    g344: Circle CenterX=371.073 CenterY=76.4095 CenterZ=0 NormalX=0 NormalY=0 NormalZ=1 AngleXU=0 Radius=1
    g345: BSplineCurve PolesCount=3 KnotsCount=2 Degree=2 IsPeriodic=0
    g346: GeomPoint X=375.073 Y=72.4095 Z=0
    g347: GeomPoint X=371.073 Y=76.4095 Z=0
    g348: LineSegment StartX=322.073 StartY=76.4095 StartZ=0 EndX=371.073 EndY=76.4095 EndZ=0
  constraints (575):
    c: Coincident(g0,g2)
    c: Block(g0)
    c: Block(g1)
    c: Vertical(g3)
    c: Vertical(g4)
    c: Block(g4)
    c: Block(g3)
    c: Tangent(g5,g8) = 1.5708
    c: Tangent(g5,g7) = -1.5708
    c: Tangent(g7,g6) = -1.5708
    c: Tangent(g8,g6) = 1.5708
    c: Vertical(g7)
    c: Equal(g5,g6)
    c: Block(g8)
    c: Block(g7)
    c: Tangent(g9,g10) = 1.5708
    c: Tangent(g10,g12) = 1.5708
    c: Equal(g9,g12)
    c: Coincident(g11,g9)
    c: Coincident(g11,g12)
    c: Block(g10)
    c: Block(g11)
    c: Weight(g13) = 1
    c: Equal(g13,g14)
    c: Equal(g13,g15)
    c: InternalAlignment(g13,g16)
    c: InternalAlignment(g14,g16)
    c: InternalAlignment(g15,g16)
    c: InternalAlignment(g17,g16)
    c: InternalAlignment(g18,g16)
    c: Weight(g19) = 1
    c: Equal(g19,g20)
    c: Equal(g19,g21)
    c: InternalAlignment(g19,g22)
    c: InternalAlignment(g20,g22)
    c: InternalAlignment(g21,g22)
    c: InternalAlignment(g23,g22)
    c: InternalAlignment(g24,g22)
    c: Block(g22)
    c: Block(g16)
    c: Weight(g25) = 1
    c: Equal(g25,g26)
    c: Equal(g25,g27)
    c: InternalAlignment(g25,g28)
    c: InternalAlignment(g26,g28)
    c: InternalAlignment(g27,g28)
    c: InternalAlignment(g29,g28)
    c: InternalAlignment(g30,g28)
    c: Weight(g31) = 1
    c: Equal(g31,g32)
    c: Equal(g31,g33)
    c: InternalAlignment(g31,g34)
    c: InternalAlignment(g32,g34)
    c: InternalAlignment(g33,g34)
    c: InternalAlignment(g35,g34)
    c: InternalAlignment(g36,g34)
    c: Block(g34)
    c: Block(g28)
    c: Weight(g37) = 1
    c: Equal(g37,g38)
    c: Equal(g37,g39)
    c: InternalAlignment(g37,g40)
    c: InternalAlignment(g38,g40)
    c: InternalAlignment(g39,g40)
    c: InternalAlignment(g41,g40)
    c: InternalAlignment(g42,g40)
    c: Weight(g43) = 1
    c: Equal(g43,g44)
    c: Equal(g43,g45)
    c: InternalAlignment(g43,g46)
    c: InternalAlignment(g44,g46)
    c: InternalAlignment(g45,g46)
    c: InternalAlignment(g47,g46)
    c: InternalAlignment(g48,g46)
    c: Block(g40)
    c: Block(g46)
    c: Coincident(g49,g4)
    c: Coincident(g49,g3)
    c: Horizontal(g49)
    c: Distance(g49) = 450
    c: Coincident(g50,g4)
    c: Coincident(g50,g3)
    c: Horizontal(g50)
    c: Horizontal(g51)
    c: Coincident(g2,g51)
    c: Block(g51)
    c: Coincident(g1,g51)
    c: Weight(g52) = 1
    c: Equal(g52,g53)
    c: Equal(g52,g54)
    c: InternalAlignment(g52,g55)
    c: InternalAlignment(g53,g55)
    c: InternalAlignment(g54,g55)
    c: InternalAlignment(g56,g55)
    c: InternalAlignment(g57,g55)
    c: Block(g55)
    c: Weight(g58) = 1
    c: Equal(g58,g59)
    c: Equal(g58,g60)
    c: InternalAlignment(g58,g61)
    c: InternalAlignment(g59,g61)
    c: InternalAlignment(g60,g61)
    c: InternalAlignment(g62,g61)
    c: InternalAlignment(g63,g61)
    c: Block(g61)
    c: Weight(g64) = 1
    c: Equal(g64,g65)
    c: Equal(g64,g66)
    c: InternalAlignment(g64,g67)
    c: InternalAlignment(g65,g67)
    c: InternalAlignment(g66,g67)
    c: InternalAlignment(g68,g67)
    c: InternalAlignment(g69,g67)
    c: Block(g67)
    c: Weight(g70) = 1
    c: Equal(g70,g71)
    c: Equal(g70,g72)
    c: InternalAlignment(g70,g73)
    c: InternalAlignment(g71,g73)
    c: InternalAlignment(g72,g73)
    c: InternalAlignment(g74,g73)
    c: InternalAlignment(g75,g73)
    c: Block(g73)
    c: Weight(g76) = 1
    c: Equal(g76,g77)
    c: Equal(g76,g78)
    c: InternalAlignment(g76,g79)
    c: InternalAlignment(g77,g79)
    c: InternalAlignment(g78,g79)
    c: InternalAlignment(g80,g79)
    c: InternalAlignment(g81,g79)
    c: Weight(g82) = 1
    c: Equal(g82,g83)
    c: Equal(g82,g84)
    c: InternalAlignment(g82,g85)
    c: InternalAlignment(g83,g85)
    c: InternalAlignment(g84,g85)
    c: InternalAlignment(g86,g85)
    c: InternalAlignment(g87,g85)
    c: Block(g79)
    c: Block(g85)
    c: Coincident(g88,g79)
    c: Coincident(g88,g85)
    c: Vertical(g88)
    c: Coincident(g89,g79)
    c: Coincident(g89,g61)
    c: Coincident(g90,g61)
    c: Coincident(g90,g85)
    c: Weight(g91) = 1
    c: Equal(g91,g92)
    c: Equal(g91,g93)
    c: InternalAlignment(g91,g94)
    c: InternalAlignment(g92,g94)
    c: InternalAlignment(g93,g94)
    c: InternalAlignment(g95,g94)
    c: InternalAlignment(g96,g94)
    c: Weight(g97) = 1
    c: Equal(g97,g98)
    c: Equal(g97,g99)
    c: InternalAlignment(g97,g100)
    c: InternalAlignment(g98,g100)
    c: InternalAlignment(g99,g100)
    c: InternalAlignment(g101,g100)
    c: InternalAlignment(g102,g100)
    c: Block(g94)
    c: Block(g100)
    c: Coincident(g103,g94)
    c: Coincident(g103,g100)
    c: Vertical(g103)
    c: Coincident(g104,g94)
    c: Coincident(g104,g55)
    c: Coincident(g105,g55)
    c: Coincident(g105,g100)
    c: Weight(g106) = 1
    c: Equal(g106,g107)
    c: Equal(g106,g108)
    c: InternalAlignment(g106,g109)
    c: InternalAlignment(g107,g109)
    c: InternalAlignment(g108,g109)
    c: InternalAlignment(g110,g109)
    c: InternalAlignment(g111,g109)
    c: Weight(g112) = 1
    c: Equal(g112,g113)
    c: Equal(g112,g114)
    c: InternalAlignment(g112,g115)
    c: InternalAlignment(g113,g115)
    c: InternalAlignment(g114,g115)
    c: InternalAlignment(g116,g115)
    c: InternalAlignment(g117,g115)
    c: Block(g109)
    c: Block(g115)
    c: Coincident(g118,g109)
    c: Coincident(g118,g115)
    c: Vertical(g118)
    c: Coincident(g119,g115)
    c: Coincident(g119,g73)
    c: Coincident(g120,g73)
    c: Coincident(g120,g109)
    c: Weight(g121) = 1
    c: Equal(g121,g122)
    c: Equal(g121,g123)
    c: InternalAlignment(g121,g124)
    c: InternalAlignment(g122,g124)
    c: InternalAlignment(g123,g124)
    c: InternalAlignment(g125,g124)
    c: InternalAlignment(g126,g124)
    c: Weight(g127) = 1
    c: Equal(g127,g128)
    c: Equal(g127,g129)
    c: InternalAlignment(g127,g130)
    c: InternalAlignment(g128,g130)
    c: InternalAlignment(g129,g130)
    c: InternalAlignment(g131,g130)
    c: InternalAlignment(g132,g130)
    c: Block(g124)
    c: Block(g130)
    c: Coincident(g133,g124)
    c: Coincident(g133,g130)
    c: Vertical(g133)
    c: Coincident(g134,g130)
    c: Coincident(g134,g67)
    c: Coincident(g135,g67)
    c: Coincident(g135,g124)
    c: Weight(g136) = 1
    c: Equal(g136,g137)
    c: Equal(g136,g138)
    c: InternalAlignment(g136,g139)
    c: InternalAlignment(g137,g139)
    c: InternalAlignment(g138,g139)
    c: InternalAlignment(g140,g139)
    c: InternalAlignment(g141,g139)
    c: Weight(g142) = 1
    c: Equal(g142,g143)
    c: Equal(g142,g144)
    c: InternalAlignment(g142,g145)
    c: InternalAlignment(g143,g145)
    c: InternalAlignment(g144,g145)
    c: InternalAlignment(g146,g145)
    c: InternalAlignment(g147,g145)
    c: Weight(g148) = 1
    c: Equal(g148,g149)
    c: Equal(g148,g150)
    c: InternalAlignment(g148,g151)
    c: InternalAlignment(g149,g151)
    c: InternalAlignment(g150,g151)
    c: InternalAlignment(g152,g151)
    c: InternalAlignment(g153,g151)
    c: Weight(g154) = 1
    c: Equal(g154,g155)
    c: Equal(g154,g156)
    c: InternalAlignment(g154,g157)
    c: InternalAlignment(g155,g157)
    c: InternalAlignment(g156,g157)
    c: InternalAlignment(g158,g157)
    c: InternalAlignment(g159,g157)
    c: Block(g157)
    c: Block(g151)
    c: Block(g145)
    c: Block(g139)
    c: Coincident(g160,g34)
    c: Coincident(g160,g157)
    c: Coincident(g161,g157)
    c: Coincident(g161,g151)
    c: Horizontal(g161)
    c: Coincident(g162,g151)
    c: Coincident(g162,g34)
    c: Vertical(g162)
    c: Coincident(g163,g28)
    c: Coincident(g163,g145)
    c: Vertical(g163)
    c: Coincident(g164,g145)
    c: Coincident(g164,g139)
    c: Horizontal(g164)
    c: Coincident(g165,g139)
    c: Coincident(g165,g28)
    c: Weight(g166) = 1
    c: Equal(g166,g167)
    c: Equal(g166,g168)
    c: InternalAlignment(g166,g169)
    c: InternalAlignment(g167,g169)
    c: InternalAlignment(g168,g169)
    c: InternalAlignment(g170,g169)
    c: InternalAlignment(g171,g169)
    c: Weight(g172) = 1
    c: Equal(g172,g173)
    c: Equal(g172,g174)
    c: InternalAlignment(g172,g175)
    c: InternalAlignment(g173,g175)
    c: InternalAlignment(g174,g175)
    c: InternalAlignment(g176,g175)
    c: InternalAlignment(g177,g175)
    c: Weight(g178) = 1
    c: Equal(g178,g179)
    c: Equal(g178,g180)
    c: InternalAlignment(g178,g181)
    c: InternalAlignment(g179,g181)
    c: InternalAlignment(g180,g181)
    c: InternalAlignment(g182,g181)
    c: InternalAlignment(g183,g181)
    c: Weight(g184) = 1
    c: Equal(g184,g185)
    c: Equal(g184,g186)
    c: InternalAlignment(g184,g187)
    c: InternalAlignment(g185,g187)
    c: InternalAlignment(g186,g187)
    c: InternalAlignment(g188,g187)
    c: InternalAlignment(g189,g187)
    c: Block(g187)
    c: Block(g181)
    c: Block(g175)
    c: Block(g169)
    c: Coincident(g190,g187)
    c: Coincident(g190,g181)
    c: Horizontal(g190)
    c: Coincident(g191,g181)
    c: Coincident(g191,g16)
    c: Vertical(g191)
    c: Coincident(g192,g22)
    c: Coincident(g192,g175)
    c: Vertical(g192)
    c: Coincident(g193,g175)
    c: Coincident(g193,g169)
    c: Horizontal(g193)
    c: Coincident(g194,g169)
    c: Coincident(g194,g22)
    c: Coincident(g195,g16)
    c: Weight(g196) = 1
    c: Equal(g196,g197)
    c: Equal(g196,g198)
    c: InternalAlignment(g196,g199)
    c: InternalAlignment(g197,g199)
    c: InternalAlignment(g198,g199)
    c: InternalAlignment(g200,g199)
    c: InternalAlignment(g201,g199)
    c: Weight(g202) = 1
    c: Equal(g202,g203)
    c: Equal(g202,g204)
    c: InternalAlignment(g202,g205)
    c: InternalAlignment(g203,g205)
    c: InternalAlignment(g204,g205)
    c: InternalAlignment(g206,g205)
    c: InternalAlignment(g207,g205)
    c: Block(g205)
    c: Block(g199)
    c: Coincident(g208,g205)
    c: Coincident(g208,g40)
    c: Coincident(g209,g40)
    c: Coincident(g209,g199)
    c: Coincident(g210,g199)
    c: Coincident(g210,g205)
    c: Vertical(g210)
    c: Weight(g211) = 1
    c: Equal(g211,g212)
    c: Equal(g211,g213)
    c: InternalAlignment(g211,g214)
    c: InternalAlignment(g212,g214)
    c: InternalAlignment(g213,g214)
    c: InternalAlignment(g215,g214)
    c: InternalAlignment(g216,g214)
    c: Weight(g217) = 1
    c: Equal(g217,g218)
    c: Equal(g217,g219)
    c: InternalAlignment(g217,g220)
    c: InternalAlignment(g218,g220)
    c: InternalAlignment(g219,g220)
    c: InternalAlignment(g221,g220)
    c: InternalAlignment(g222,g220)
    c: Block(g220)
    c: Block(g214)
    c: Coincident(g223,g214)
    c: Coincident(g223,g46)
    c: Coincident(g224,g46)
    c: Coincident(g224,g220)
    c: Coincident(g225,g220)
    c: Coincident(g225,g214)
    c: Vertical(g225)
    c: Horizontal(g226)
    c: Block(g226)
    c: Vertical(g227)
    c: Block(g227)
    c: Block(g228)
    c: Weight(g229) = 1
    c: Equal(g229,g230)
    c: Equal(g229,g231)
    c: InternalAlignment(g229,g232)
    c: InternalAlignment(g230,g232)
    c: InternalAlignment(g231,g232)
    c: InternalAlignment(g233,g232)
    c: InternalAlignment(g234,g232)
    c: Weight(g235) = 1
    c: Equal(g235,g236)
    c: Equal(g235,g237)
    c: InternalAlignment(g235,g238)
    c: InternalAlignment(g236,g238)
    c: InternalAlignment(g237,g238)
    c: InternalAlignment(g239,g238)
    c: InternalAlignment(g240,g238)
    c: Weight(g241) = 1
    c: Equal(g241,g242)
    c: Equal(g241,g243)
    c: InternalAlignment(g241,g244)
    c: InternalAlignment(g242,g244)
    c: InternalAlignment(g243,g244)
    c: InternalAlignment(g245,g244)
    c: InternalAlignment(g246,g244)
    c: Weight(g247) = 1
    c: Equal(g247,g248)
    c: Equal(g247,g249)
    c: InternalAlignment(g247,g250)
    c: InternalAlignment(g248,g250)
    c: InternalAlignment(g249,g250)
    c: InternalAlignment(g251,g250)
    c: InternalAlignment(g252,g250)
    c: Block(g232)
    c: Block(g238)
    c: Block(g244)
    c: Block(g250)
    c: Coincident(g253,g238)
    c: Coincident(g253,g232)
    c: Horizontal(g253)
    c: Block(g195)
    c: Weight(g254) = 1
    c: Equal(g254,g255)
    c: Equal(g254,g256)
    c: InternalAlignment(g254,g257)
    c: InternalAlignment(g255,g257)
    c: InternalAlignment(g256,g257)
    c: InternalAlignment(g258,g257)
    c: InternalAlignment(g259,g257)
    c: Weight(g260) = 1
    c: Equal(g260,g261)
    c: Equal(g260,g262)
    c: InternalAlignment(g260,g263)
    c: InternalAlignment(g261,g263)
    c: InternalAlignment(g262,g263)
    c: InternalAlignment(g264,g263)
    c: InternalAlignment(g265,g263)
    c: Block(g257)
    c: Block(g263)
    c: Coincident(g336,g257)
    c: Coincident(g266,g257)
    c: Coincident(g266,g263)
    c: Weight(g267) = 1
    c: Equal(g267,g268)
    c: Equal(g267,g269)
    c: InternalAlignment(g267,g270)
    c: InternalAlignment(g268,g270)
    c: InternalAlignment(g269,g270)
    c: InternalAlignment(g271,g270)
    c: InternalAlignment(g272,g270)
    c: Weight(g273) = 1
    c: Equal(g273,g274)
    c: Equal(g273,g275)
    c: InternalAlignment(g273,g276)
    c: InternalAlignment(g274,g276)
    c: InternalAlignment(g275,g276)
    c: InternalAlignment(g277,g276)
    c: InternalAlignment(g278,g276)
    c: Weight(g279) = 1
    c: Equal(g279,g280)
    c: Equal(g279,g281)
    c: InternalAlignment(g279,g282)
    c: InternalAlignment(g280,g282)
    c: InternalAlignment(g281,g282)
    c: InternalAlignment(g283,g282)
    c: InternalAlignment(g284,g282)
    c: Block(g282)
    c: Block(g276)
    c: Block(g270)
    c: Coincident(g285,g276)
    c: Coincident(g285,g270)
    c: Coincident(g286,g270)
    c: Coincident(g286,g282)
    c: Vertical(g286)
    c: Coincident(g287,g282)
    c: Coincident(g287,g276)
    c: Horizontal(g287)
    c: Weight(g288) = 1
    c: Equal(g288,g289)
    c: InternalAlignment(g288,g290)
    c: InternalAlignment(g289,g290)
    c: InternalAlignment(g291,g290)
    c: InternalAlignment(g292,g290)
    c: Weight(g293) = 1
    c: Equal(g293,g294)
    c: Equal(g293,g295)
    c: InternalAlignment(g293,g296)
    c: InternalAlignment(g294,g296)
    c: InternalAlignment(g295,g296)
    c: InternalAlignment(g297,g296)
    c: InternalAlignment(g298,g296)
    c: Weight(g299) = 1
    c: Equal(g299,g300)
    c: Equal(g299,g301)
    c: InternalAlignment(g299,g302)
    c: InternalAlignment(g300,g302)
    c: InternalAlignment(g301,g302)
    c: InternalAlignment(g303,g302)
    c: InternalAlignment(g304,g302)
    c: Equal(g305,g306)
    c: Equal(g305,g307)
    c: InternalAlignment(g305,g308)
    c: InternalAlignment(g306,g308)
    c: InternalAlignment(g307,g308)
    c: InternalAlignment(g309,g308)
    c: InternalAlignment(g310,g308)
    c: Block(g296)
    c: Block(g302)
    c: Block(g308)
    c: Block(g290)
    c: Coincident(g311,g290)
    c: Coincident(g311,g296)
    c: Horizontal(g311)
    c: Coincident(g312,g296)
    c: Coincident(g312,g302)
    c: Vertical(g312)
    c: Coincident(g313,g302)
    c: Coincident(g313,g308)
    c: Horizontal(g313)
    c: Coincident(g314,g308)
    c: Coincident(g314,g290)
    c: Weight(g315) = 1
    c: Equal(g315,g316)
    c: Equal(g315,g317)
    c: InternalAlignment(g315,g318)
    c: InternalAlignment(g316,g318)
    c: InternalAlignment(g317,g318)
    c: InternalAlignment(g319,g318)
    c: InternalAlignment(g320,g318)
    c: Weight(g321) = 1
    c: Equal(g321,g322)
    c: Equal(g321,g323)
    c: InternalAlignment(g321,g324)
    c: InternalAlignment(g322,g324)
    c: InternalAlignment(g323,g324)
    c: InternalAlignment(g325,g324)
    c: InternalAlignment(g326,g324)
    c: Weight(g327) = 1
    c: Equal(g327,g328)
    c: Equal(g327,g329)
    c: InternalAlignment(g327,g330)
    c: InternalAlignment(g328,g330)
    c: InternalAlignment(g329,g330)
    c: InternalAlignment(g331,g330)
    c: InternalAlignment(g332,g330)
    c: Block(g330)
    c: Block(g324)
    c: Block(g318)
    c: Coincident(g333,g330)
    c: Coincident(g333,g324)
    c: Horizontal(g333)
    c: Coincident(g334,g324)
    c: Coincident(g334,g318)
    c: Vertical(g334)
    c: Coincident(g335,g318)
    c: Coincident(g335,g330)
    c: InternalAlignment(g337,g338)
    c: InternalAlignment(g339,g338)
    c: InternalAlignment(g340,g338)
    c: Block(g338)
    c: Horizontal(g341)
    c: Distance(g341) = 4
    c: Equal(g342,g343)
    c: Equal(g342,g344)
    c: InternalAlignment(g342,g345)
    c: InternalAlignment(g343,g345)
    c: InternalAlignment(g344,g345)
    c: InternalAlignment(g346,g345)
    c: InternalAlignment(g347,g345)
    c: Block(g345)
    c: Coincident(g347,g341)
    c: Coincident(g348,g338)
    c: Coincident(g348,g341)
    c: Horizontal(g348)
    c: Block(g348)
FEATURE [Sketcher::SketchObject] Sketch001
  FullyConstrained = true
  MapMode = 4
  Placement = pos=(0,0,0) rot=(0.57735,0.57735,0.57735;2.0944rad)
  Support = -> [Sketch]
  sketch-geometry (46):
    g0: BSplineCurve PolesCount=3 KnotsCount=2 Degree=2 IsPeriodic=0
    g1: ArcOfCircle CenterX=73.1223 CenterY=-32.291 CenterZ=0 NormalX=0 NormalY=0 NormalZ=1 AngleXU=0 Radius=13 StartAngle=5.92268 EndAngle=9.06428
    g2: ArcOfCircle CenterX=66.7816 CenterY=-49.1439 CenterZ=0 NormalX=0 NormalY=0 NormalZ=1 AngleXU=0 Radius=13 StartAngle=2.78068 EndAngle=5.92131
    g3: ArcOfCircle CenterX=55.9263 CenterY=-78.1807 CenterZ=0 NormalX=0 NormalY=0 NormalZ=1 AngleXU=0 Radius=13 StartAngle=5.92268 EndAngle=9.06428
    g4: ArcOfCircle CenterX=49.5884 CenterY=-95.0342 CenterZ=0 NormalX=0 NormalY=0 NormalZ=1 AngleXU=0 Radius=13 StartAngle=2.78068 EndAngle=5.92131
    g5: ArcOfCircle CenterX=38.7206 CenterY=-124.067 CenterZ=0 NormalX=0 NormalY=0 NormalZ=1 AngleXU=0 Radius=13 StartAngle=5.92268 EndAngle=9.06428
    g6: ArcOfCircle CenterX=32.3875 CenterY=-140.92 CenterZ=0 NormalX=0 NormalY=0 NormalZ=1 AngleXU=0 Radius=13 StartAngle=2.78068 EndAngle=5.92131
    g7: ArcOfCircle CenterX=21.4715 CenterY=-169.934 CenterZ=0 NormalX=0 NormalY=0 NormalZ=1 AngleXU=0 Radius=13 StartAngle=5.92268 EndAngle=9.06428
    g8: ArcOfCircle CenterX=15.1336 CenterY=-186.787 CenterZ=0 NormalX=0 NormalY=0 NormalZ=1 AngleXU=0 Radius=13 StartAngle=2.78068 EndAngle=5.92131
    g9-g12: Circle x4 (B-spline internal-alignment scaffolding for g13; pole/knot coordinates omitted)
    g13: BSplineCurve PolesCount=4 KnotsCount=2 Degree=3 IsPeriodic=0
    g14: GeomPoint X=28.8094 Y=-19.0875 Z=0
    g15: GeomPoint X=47.0443 Y=-50.4712 Z=0
    g16: Circle CenterX=53.5586 CenterY=-23.2695 CenterZ=0 NormalX=0 NormalY=0 NormalZ=1 AngleXU=0 Radius=3.24518
    g17: Circle CenterX=-195.441 CenterY=-127.082 CenterZ=0 NormalX=0 NormalY=0 NormalZ=1 AngleXU=0 Radius=1
    g18: Circle CenterX=-8.24091 CenterY=-197.481 CenterZ=0 NormalX=0 NormalY=0 NormalZ=1 AngleXU=0 Radius=1
    g19: Circle CenterX=12.8789 CenterY=-141.321 CenterZ=0 NormalX=0 NormalY=0 NormalZ=1 AngleXU=0 Radius=1
    g20: BSplineCurve PolesCount=3 KnotsCount=2 Degree=2 IsPeriodic=0
    g21: GeomPoint X=-195.441 Y=-127.082 Z=0
    g22: GeomPoint X=12.8789 Y=-141.321 Z=0
    g23: Circle CenterX=-12.8016 CenterY=-179.036 CenterZ=0 NormalX=0 NormalY=0 NormalZ=1 AngleXU=0 Radius=10.5072
    g24: Circle CenterX=0.933922 CenterY=-166.43 CenterZ=0 NormalX=0 NormalY=0 NormalZ=1 AngleXU=0 Radius=3.26661
    g25: Circle CenterX=-33.5518 CenterY=-176.44 CenterZ=0 NormalX=0 NormalY=0 NormalZ=1 AngleXU=0 Radius=5.64388
    g26: Circle CenterX=-47.2366 CenterY=-173.859 CenterZ=0 NormalX=0 NormalY=0 NormalZ=1 AngleXU=0 Radius=3.01653
    g27: Circle CenterX=-56.2595 CenterY=-171.456 CenterZ=0 NormalX=0 NormalY=0 NormalZ=1 AngleXU=0 Radius=2.12826
    g28: ArcOfCircle CenterX=51.2151 CenterY=-198.473 CenterZ=0 NormalX=0 NormalY=0 NormalZ=1 AngleXU=0 Radius=20 StartAngle=2.78189 EndAngle=4.35269
    g29: LineSegment StartX=32.4951 StartY=-191.433 StartZ=0 EndX=94.6578 EndY=-26.1352 EndZ=0
    g30: LineSegment StartX=43.1192 StartY=-220.001 StartZ=0 EndX=-196.497 EndY=-129.89 EndZ=0
    g31: LineSegment StartX=43.1192 StartY=-220.001 StartZ=0 EndX=44.1752 EndY=-217.193 EndZ=0
    g32: LineSegment StartX=117.223 StartY=-19.0875 StartZ=0 EndX=117.223 EndY=-16.0875 EndZ=0
    g33: LineSegment StartX=117.223 StartY=-16.0875 StartZ=0 EndX=17.2232 EndY=-16.0875 EndZ=0
    g34: LineSegment StartX=17.2232 StartY=-16.0875 StartZ=0 EndX=17.2232 EndY=-19.0875 EndZ=0
    g35: LineSegment StartX=28.8094 StartY=-19.0875 StartZ=0 EndX=17.2232 EndY=-19.0875 EndZ=0
    g36: LineSegment StartX=47.0443 StartY=-50.4712 StartZ=0 EndX=12.8789 EndY=-141.321 EndZ=0
    g37: LineSegment StartX=-195.441 StartY=-127.082 StartZ=0 EndX=-196.497 EndY=-129.89 EndZ=0
    g38: LineSegment StartX=85.2866 StartY=-36.8766 StartZ=0 EndX=78.9396 EndY=-53.7463 EndZ=0
    g39: LineSegment StartX=60.9579 StartY=-27.7053 StartZ=0 EndX=54.6191 EndY=-44.5532 EndZ=0
    g40: LineSegment StartX=68.0907 StartY=-82.7664 StartZ=0 EndX=61.7465 EndY=-99.6365 EndZ=0
    g41: LineSegment StartX=43.7619 StartY=-73.595 StartZ=0 EndX=37.426 EndY=-90.4435 EndZ=0
    g42: LineSegment StartX=50.885 StartY=-128.652 StartZ=0 EndX=44.5456 EndY=-145.522 EndZ=0
    g43: LineSegment StartX=26.5562 StartY=-119.481 StartZ=0 EndX=20.2251 EndY=-136.329 EndZ=0
    g44: LineSegment StartX=9.3071 StartY=-165.349 StartZ=0 EndX=2.97115 EndY=-182.197 EndZ=0
    g45: LineSegment StartX=33.6358 StartY=-174.52 StartZ=0 EndX=27.2917 EndY=-191.39 EndZ=0
  constraints (71):
    c: Block(g0)
    c: Block(g1)
    c: Block(g2)
    c: Block(g4)
    c: Block(g3)
    c: Block(g6)
    c: Block(g5)
    c: Block(g8)
    c: Block(g7)
    c: Weight(g9) = 1
    c: Equal(g9,g10)
    c: Equal(g9,g11)
    c: Equal(g9,g12)
    c: InternalAlignment(g9-g12 -> g13) x4
    c: InternalAlignment(g14,g13)
    c: InternalAlignment(g15,g13)
    c: Block(g16)
    c: Weight(g17) = 1
    c: Equal(g17,g18)
    c: Equal(g17,g19)
    c: InternalAlignment(g17,g20)
    c: InternalAlignment(g18,g20)
    c: InternalAlignment(g19,g20)
    c: InternalAlignment(g21,g20)
    c: InternalAlignment(g22,g20)
    c: Block(g20)
    c: Block(g23)
    c: Block(g24)
    c: Block(g25)
    c: Block(g26)
    c: Block(g27)
    c: Block(g28)
    c: Coincident(g29,g28)
    c: Coincident(g29,g0)
    c: Block(g13)
    c: Coincident(g31,g30)
    c: Coincident(g31,g28)
    c: Block(g31)
    c: Coincident(g32,g0)
    c: Vertical(g32)
    c: Coincident(g33,g32)
    c: Horizontal(g33)
    c: Coincident(g34,g33)
    c: Vertical(g34)
    c: Block(g33)
    c: Coincident(g35,g13)
    c: Coincident(g35,g34)
    c: Horizontal(g35)
    c: Coincident(g36,g13)
    c: Coincident(g36,g20)
    c: Coincident(g37,g20)
    c: Coincident(g37,g30)
    c: Block(g30)
    c: Coincident(g38,g1)
    c: Coincident(g38,g2)
    c: Coincident(g39,g1)
    c: Coincident(g39,g2)
    c: Coincident(g40,g3)
    c: Coincident(g40,g4)
    c: Coincident(g41,g3)
    c: Coincident(g41,g4)
    c: Coincident(g42,g5)
    c: Coincident(g42,g6)
    c: Coincident(g43,g5)
    c: Coincident(g43,g6)
    c: Coincident(g44,g7)
    c: Coincident(g44,g8)
    c: Coincident(g45,g7)
    c: Coincident(g45,g8)
    c: Distance(g30) = 256
    c: Distance(g33) = 100
FEATURE [Part::Extrusion] Extrude002
  Base = -> Sketch001
  Dir = (1,0,0)
  DirMode = 2
  FaceMakerClass = Part::FaceMakerBullseye
  LengthFwd = 8
  LengthRev = 0
  Solid = true
  Symmetric = false
FEATURE [Sketcher::SketchObject] Sketch002
  FullyConstrained = true
  sketch-geometry (20):
    g0: LineSegment StartX=-2.77179 StartY=-200.304 StartZ=0 EndX=5.22821 EndY=-200.304 EndZ=0
    g1: LineSegment StartX=5.22821 StartY=-200.304 StartZ=0 EndX=5.22821 EndY=-197.304 EndZ=0
    g2: LineSegment StartX=-2.77179 StartY=-200.304 StartZ=0 EndX=-2.77179 EndY=-197.304 EndZ=0
    g3: LineSegment StartX=5.22821 StartY=-197.304 StartZ=0 EndX=8.22821 EndY=-197.304 EndZ=0
    g4: LineSegment StartX=-2.77179 StartY=-197.304 StartZ=0 EndX=-5.77179 EndY=-197.304 EndZ=0
    g5: LineSegment StartX=19.2282 StartY=-203.304 StartZ=0 EndX=19.2282 EndY=-206.304 EndZ=0
    g6: LineSegment StartX=-16.7718 StartY=-203.304 StartZ=0 EndX=-16.7718 EndY=-206.304 EndZ=0
    g7: LineSegment StartX=-16.7718 StartY=-206.304 StartZ=0 EndX=19.2282 EndY=-206.304 EndZ=0
    g8: Circle CenterX=-16.7718 CenterY=-203.304 CenterZ=0 NormalX=0 NormalY=0 NormalZ=1 AngleXU=0 Radius=1
    g9: Circle CenterX=-5.77179 CenterY=-203.304 CenterZ=0 NormalX=0 NormalY=0 NormalZ=1 AngleXU=0 Radius=1
    g10: Circle CenterX=-5.77179 CenterY=-197.304 CenterZ=0 NormalX=0 NormalY=0 NormalZ=1 AngleXU=0 Radius=1
    g11: BSplineCurve PolesCount=3 KnotsCount=2 Degree=2 IsPeriodic=0
    g12: GeomPoint X=-16.7718 Y=-203.304 Z=0
    g13: GeomPoint X=-5.77179 Y=-197.304 Z=0
    g14: Circle CenterX=19.2282 CenterY=-203.304 CenterZ=0 NormalX=0 NormalY=0 NormalZ=1 AngleXU=0 Radius=1
    g15: Circle CenterX=8.22821 CenterY=-203.304 CenterZ=0 NormalX=0 NormalY=0 NormalZ=1 AngleXU=0 Radius=1
    g16: Circle CenterX=8.22821 CenterY=-197.304 CenterZ=0 NormalX=0 NormalY=0 NormalZ=1 AngleXU=0 Radius=1
    g17: BSplineCurve PolesCount=3 KnotsCount=2 Degree=2 IsPeriodic=0
    g18: GeomPoint X=19.2282 Y=-203.304 Z=0
    g19: GeomPoint X=8.22821 Y=-197.304 Z=0
  constraints (41):
    c: Horizontal(g0)
    c: Distance(g0) = 8
    c: Coincident(g1,g0)
    c: Vertical(g1)
    c: Distance(g1) = 3
    c: Coincident(g2,g0)
    c: Vertical(g2)
    c: Distance(g2) = 3
    c: Coincident(g3,g1)
    c: Horizontal(g3)
    c: Distance(g3) = 3
    c: Coincident(g4,g2)
    c: Horizontal(g4)
    c: Distance(g4) = 3
    c: Vertical(g5)
    c: Vertical(g6)
    c: Coincident(g7,g6)
    c: Coincident(g7,g5)
    c: Weight(g8) = 1
    c: Equal(g8,g9)
    c: Equal(g8,g10)
    c: Coincident(g11,g4)
    c: InternalAlignment(g8,g11)
    c: InternalAlignment(g9,g11)
    c: InternalAlignment(g10,g11)
    c: InternalAlignment(g12,g11)
    c: InternalAlignment(g13,g11)
    c: Coincident(g17,g5)
    c: Weight(g14) = 1
    c: Equal(g14,g15)
    c: Equal(g14,g16)
    c: Coincident(g17,g3)
    c: InternalAlignment(g14,g17)
    c: InternalAlignment(g15,g17)
    c: InternalAlignment(g16,g17)
    c: InternalAlignment(g18,g17)
    c: InternalAlignment(g19,g17)
    c: Block(g7)
    c: Block(g17)
    c: Block(g11)
    c: Block(g6)
FEATURE [Part::Extrusion] Extrude003
  Base = -> Sketch002
  Dir = (0,0,1)
  DirMode = 2
  FaceMakerClass = Part::FaceMakerBullseye
  LengthFwd = 260
  LengthRev = 0
  Solid = true
  Symmetric = false
FEATURE [Part::Extrusion] Extrude
  Base = -> Sketch
  Dir = (0,0,1)
  DirMode = 2
  FaceMakerClass = Part::FaceMakerBullseye
  LengthFwd = 14
  LengthRev = 0
  Solid = true
  Symmetric = false
